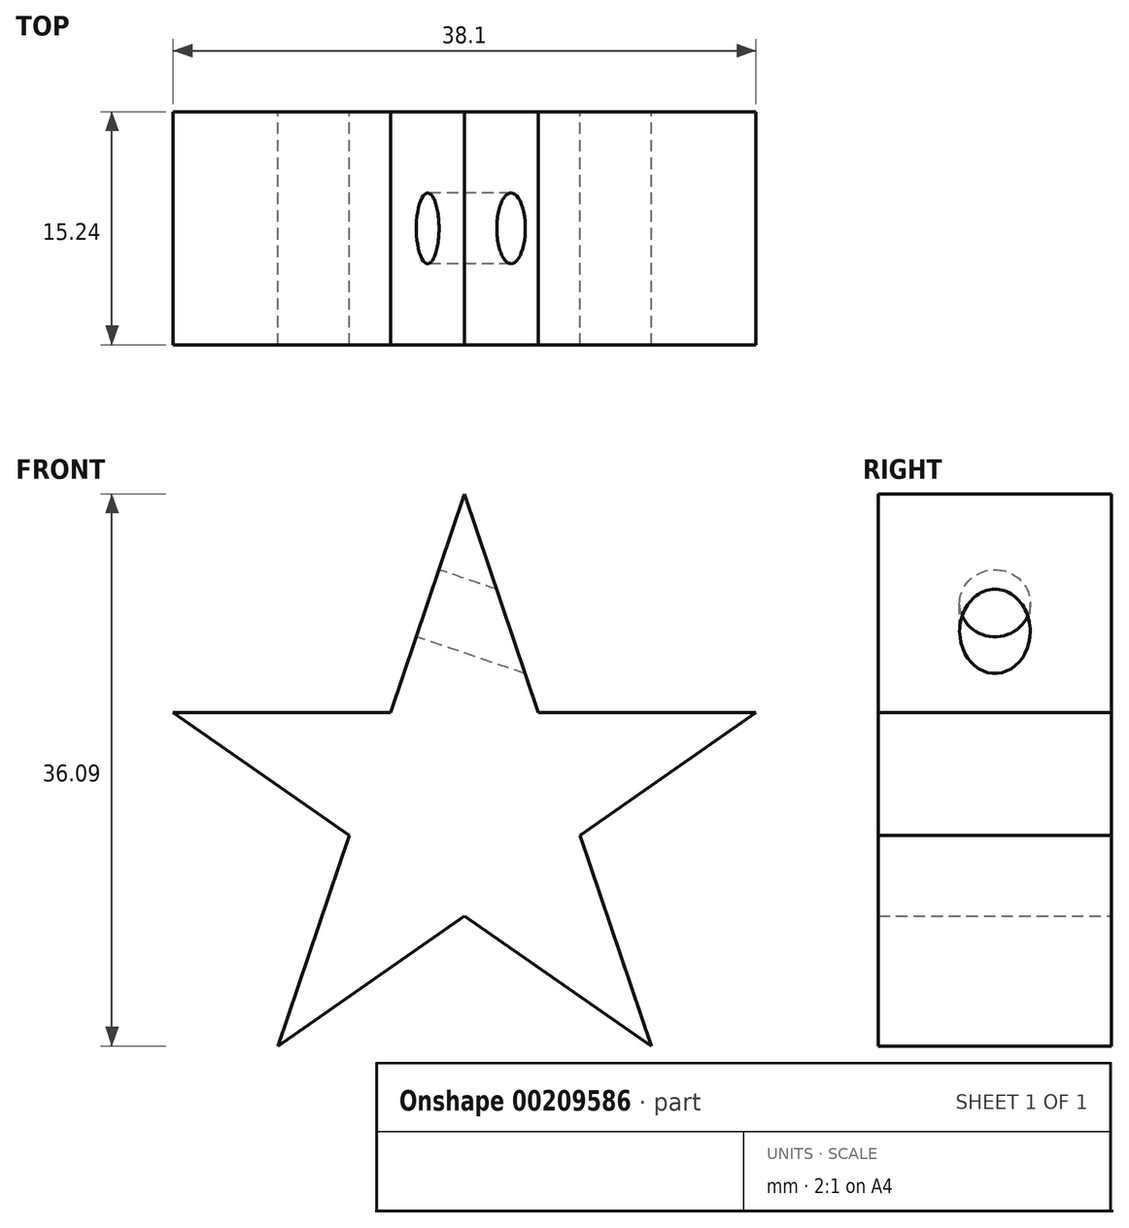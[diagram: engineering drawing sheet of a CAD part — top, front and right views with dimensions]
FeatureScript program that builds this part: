
annotation { "Feature Type Name" : "Feature", "Feature Type Description" : "" }
export const myFeature = defineFeature(function(context is Context, id is Id, definition is map)
    precondition{}
    {
        {
            var Q0;
            Q0=qCreatedBy(makeId("Front.planeOp"),FACE);
            var sketch = newSketch(context, id + "F0", { "sketchPlane" : qUnion([Q0])});
            skLineSegment(sketch, "E0", {"start": v(-12.2, 36.1) * mm, "end": v(-24.4, 0) * mm});
            skLineSegment(sketch, "E1", {"start": v(-24.4, 0) * mm, "end": v(6.85, 21.8) * mm});
            skLineSegment(sketch, "E2", {"start": v(6.85, 21.8) * mm, "end": v(-31.25, 21.8) * mm});
            skLineSegment(sketch, "E3", {"start": v(-31.25, 21.8) * mm, "end": v(0, 0) * mm});
            skLineSegment(sketch, "E4", {"start": v(0, 0) * mm, "end": v(-12.2, 36.1) * mm});
            skPoint(sketch, "E5", {"position": v(-12.2, 8.5) * mm});
            skPoint(sketch, "E6", {"position": v(-12.2, 36.1) * mm});
            skPoint(sketch, "E7", {"position": v(-14.7, 7.7) * mm});
            skSolve(sketch);
        }
        {
            var Q0;
            Q0 = qSketchRegion(id + "F0", true);
            var Q1;
            Q1 = qConstructionFilter(qBodyType(qCreatedBy(id + "F0" ,EDGE), BodyType.WIRE), ConstructionObject.NO);
            extrude(context, id + "F1", {"entities" : qUnion([Q0]), "surfaceEntities" : qUnion([Q1]), "depth" : 15.24 * mm});
        }
        {
            var Q0;
            {var subQ0=sQuery(id+"F0.wireOp",EDGE,"E4");Q0=makeQuery(id+"F1.opExtrude","SWEPT_FACE",FACE,{"disambiguationData":[OSD([subQ0]),TDD([makeQuery(id+"F0.imprint","IMPRINT",EDGE,{"disambiguationData":[TD([[makeQuery(id+"F0.imprint","INTERSECT",VERTEX,{"derivedFrom":[sQuery(id+"F0.wireOp",EDGE,"E0"),subQ0]}),1.0]])],"derivedFrom":subQ0})])]});}
            var sketch = newSketch(context, id + "F2", { "sketchPlane" : qUnion([Q0])});
            skCircle(sketch, "E8", {"center": v(-7.62, 30.56) * mm, "radius": 3.5 * mm});
            skPoint(sketch, "E9", {"position": v(-15.24, 30.56) * mm});
            skPoint(sketch, "E10", {"position": v(-7.62, 38.1) * mm});
            skSolve(sketch);
        }
        {
            var Q0;
            {var subQ0=sQuery(id+"F0.wireOp",EDGE,"E0");Q0=makeQuery(id+"F1.opExtrude","SWEPT_FACE",FACE,{"disambiguationData":[OSD([subQ0]),TDD([makeQuery(id+"F0.imprint","IMPRINT",EDGE,{"disambiguationData":[TD([[makeQuery(id+"F0.imprint","INTERSECT",VERTEX,{"derivedFrom":[subQ0,sQuery(id+"F0.wireOp",EDGE,"E4")]}),-1.0]])],"derivedFrom":subQ0})])]});}
            var sketch = newSketch(context, id + "F3", { "sketchPlane" : qUnion([Q0])});
            skCircle(sketch, "E11", {"center": v(7.62, 22.75) * mm, "radius": 2.31 * mm});
            skPoint(sketch, "E12", {"position": v(0, 22.75) * mm});
            skPoint(sketch, "E13", {"position": v(7.62, 30.3) * mm});
            skSolve(sketch);
        }
        {
            var Q0;
            Q0 = qSketchRegion(id + "F3", true);
            var Q1;
            Q1=sQuery(id+"F3.wireOp",EDGE,"E11");
            extrude(context, id + "F4", {"entities" : qUnion([Q0]), "operationType" : NewBodyOperationType.REMOVE, "surfaceEntities" : qUnion([Q1]), "oppositeDirection" : true, "depth" : 10.64 * mm});
        }
    });
